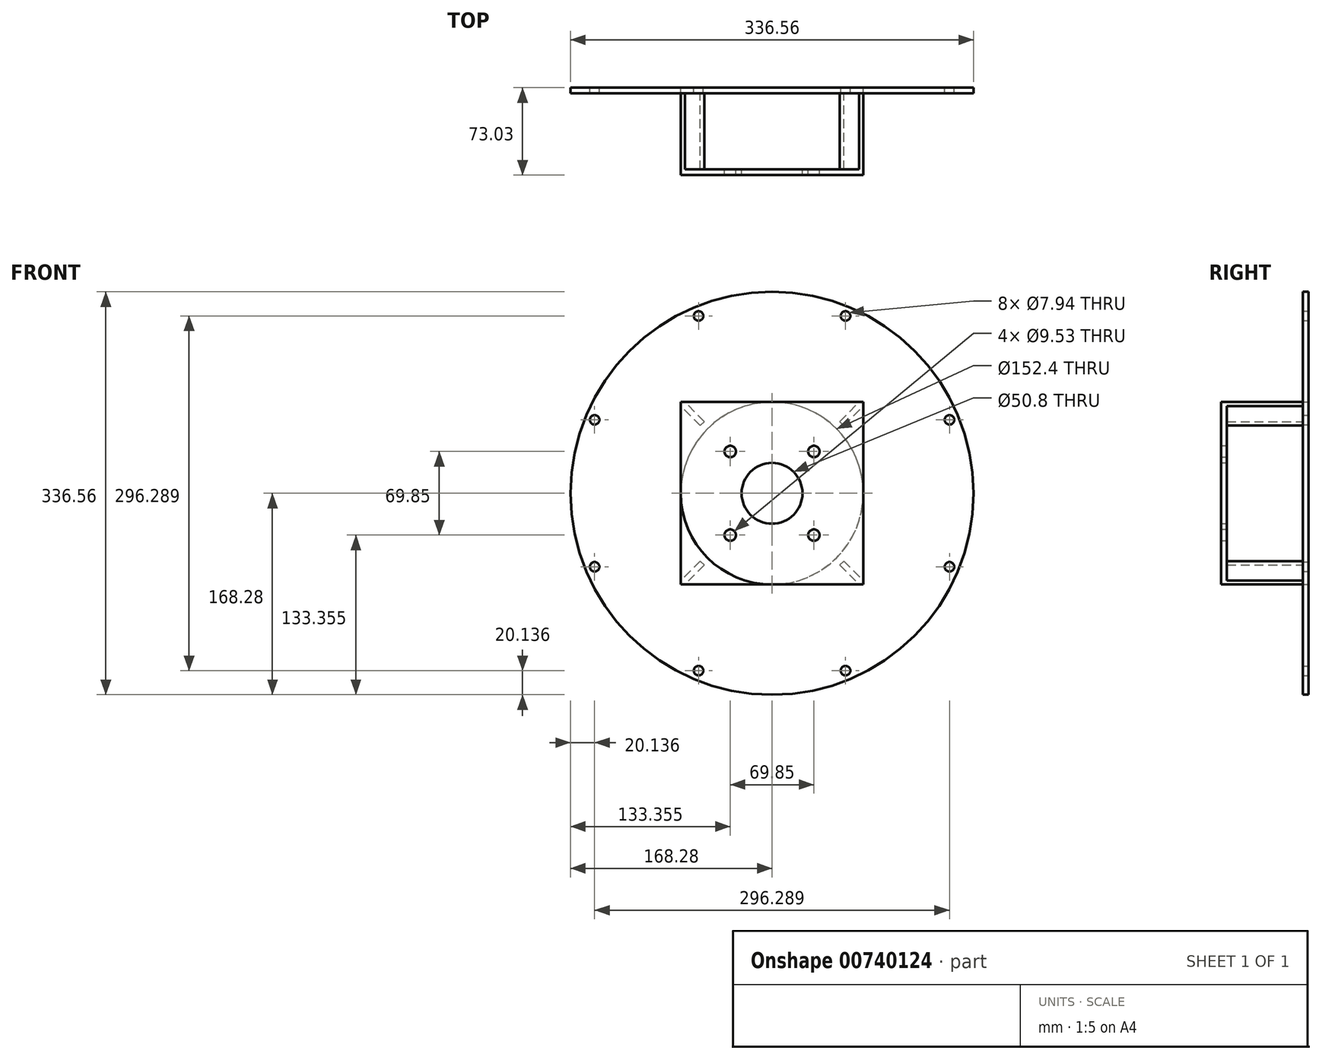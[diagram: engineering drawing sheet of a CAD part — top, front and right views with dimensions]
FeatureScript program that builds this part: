
annotation { "Feature Type Name" : "Feature", "Feature Type Description" : "" }
export const myFeature = defineFeature(function(context is Context, id is Id, definition is map)
    precondition{}
    {
        {
            var Q0;
            Q0=qCreatedBy(makeId("Front.planeOp"),FACE);
            var sketch = newSketch(context, id + "F0", { "sketchPlane" : qUnion([Q0])});
            skCircle(sketch, "E0", {"center": v(0, 0) * mm, "radius": 76.2 * mm});
            skCircle(sketch, "E1", {"center": v(0, 0) * mm, "radius": 152.4 * mm});
            skCircle(sketch, "E2", {"center": v(0, 0) * mm, "radius": 168.28 * mm});
            skLineSegment(sketch, "E3", {"start": v(0, 0) * mm, "end": v(0, -168.28) * mm});
            skLineSegment(sketch, "E4", {"start": v(64.4, -155.47) * mm, "end": v(61.36, -148.14) * mm});
            skCircle(sketch, "E5", {"center": v(61.36, -148.14) * mm, "radius": 3.97 * mm});
            skCircle(sketch, "E6.1.0", {"center": v(148.14, -61.36) * mm, "radius": 3.97 * mm});
            skCircle(sketch, "E6.2.0", {"center": v(148.14, 61.36) * mm, "radius": 3.97 * mm});
            skCircle(sketch, "E6.3.0", {"center": v(61.36, 148.14) * mm, "radius": 3.97 * mm});
            skCircle(sketch, "E6.4.0", {"center": v(-61.36, 148.14) * mm, "radius": 3.97 * mm});
            skCircle(sketch, "E6.5.0", {"center": v(-148.14, 61.36) * mm, "radius": 3.97 * mm});
            skCircle(sketch, "E6.6.0", {"center": v(-148.14, -61.36) * mm, "radius": 3.97 * mm});
            skCircle(sketch, "E6.7.0", {"center": v(-61.36, -148.14) * mm, "radius": 3.97 * mm});
            skSolve(sketch);
        }
        {
            var Q0;
            Q0=makeQuery(id+"F0.imprint","IMPRINT",FACE,{"disambiguationData":[TD([[makeQuery(id+"F0.imprint","IMPRINT",EDGE,{"derivedFrom":sQuery(id+"F0.wireOp",EDGE,"E1")}),-1.0]])]});
            var Q1;
            Q1=makeQuery(id+"F0.imprint","IMPRINT",FACE,{"disambiguationData":[TD([[makeQuery(id+"F0.imprint","IMPRINT",EDGE,{"derivedFrom":sQuery(id+"F0.wireOp",EDGE,"E0")}),-1.0]])]});
            extrude(context, id + "F1", {"entities" : qUnion([Q0, Q1]), "depth" : 4.76 * mm, "offsetDistance" : 25.4 * mm});
        }
        {
            var Q0;
            Q0=makeQuery(id+"F1.opExtrude","CAP_FACE",FACE,{"disambiguationData":[OSD([sQuery(id+"F0.wireOp",EDGE,"E0"),sQuery(id+"F0.wireOp",EDGE,"E2"),sQuery(id+"F0.wireOp",EDGE,"E5"),sQuery(id+"F0.wireOp",EDGE,"E6.1.0"),sQuery(id+"F0.wireOp",EDGE,"E6.2.0"),sQuery(id+"F0.wireOp",EDGE,"E6.3.0"),sQuery(id+"F0.wireOp",EDGE,"E6.4.0"),sQuery(id+"F0.wireOp",EDGE,"E6.5.0"),sQuery(id+"F0.wireOp",EDGE,"E6.6.0"),sQuery(id+"F0.wireOp",EDGE,"E6.7.0")])],"isStart":false});
            var sketch = newSketch(context, id + "F2", { "sketchPlane" : qUnion([Q0])});
            skLineSegment(sketch, "E7", {"start": v(0, 0) * mm, "end": v(76.2, 0) * mm});
            skLineSegment(sketch, "E8", {"start": v(76.2, 0) * mm, "end": v(76.2, 76.2) * mm});
            skLineSegment(sketch, "E9", {"start": v(76.2, 76.2) * mm, "end": v(-76.2, 76.2) * mm});
            skLineSegment(sketch, "E10", {"start": v(-76.2, 76.2) * mm, "end": v(-76.2, -76.2) * mm});
            skLineSegment(sketch, "E11", {"start": v(-76.2, -76.2) * mm, "end": v(76.2, -76.2) * mm});
            skLineSegment(sketch, "E12", {"start": v(76.2, -76.2) * mm, "end": v(76.2, 0) * mm});
            skLineSegment(sketch, "E13", {"start": v(-58.24, 58.24) * mm, "end": v(-56.56, 59.92) * mm});
            skLineSegment(sketch, "E14", {"start": v(-56.56, 59.92) * mm, "end": v(-72.83, 76.2) * mm});
            skLineSegment(sketch, "E15", {"start": v(-58.24, 58.24) * mm, "end": v(-59.92, 56.56) * mm});
            skLineSegment(sketch, "E16", {"start": v(-59.92, 56.56) * mm, "end": v(-76.2, 72.83) * mm});
            skLineSegment(sketch, "E17.1.0", {"start": v(-59.92, -56.56) * mm, "end": v(-76.2, -72.83) * mm});
            skLineSegment(sketch, "E17.1.1", {"start": v(-56.56, -59.92) * mm, "end": v(-72.83, -76.2) * mm});
            skLineSegment(sketch, "E17.1.2", {"start": v(-58.24, -58.24) * mm, "end": v(-56.56, -59.92) * mm});
            skLineSegment(sketch, "E17.1.3", {"start": v(-58.24, -58.24) * mm, "end": v(-59.92, -56.56) * mm});
            skLineSegment(sketch, "E17.2.0", {"start": v(56.56, -59.92) * mm, "end": v(72.83, -76.2) * mm});
            skLineSegment(sketch, "E17.2.1", {"start": v(59.92, -56.56) * mm, "end": v(76.2, -72.83) * mm});
            skLineSegment(sketch, "E17.2.2", {"start": v(58.24, -58.24) * mm, "end": v(59.92, -56.56) * mm});
            skLineSegment(sketch, "E17.2.3", {"start": v(58.24, -58.24) * mm, "end": v(56.56, -59.92) * mm});
            skLineSegment(sketch, "E17.3.0", {"start": v(59.92, 56.56) * mm, "end": v(76.2, 72.83) * mm});
            skLineSegment(sketch, "E17.3.1", {"start": v(56.56, 59.92) * mm, "end": v(72.83, 76.2) * mm});
            skLineSegment(sketch, "E17.3.2", {"start": v(58.24, 58.24) * mm, "end": v(56.56, 59.92) * mm});
            skLineSegment(sketch, "E17.3.3", {"start": v(58.24, 58.24) * mm, "end": v(59.92, 56.56) * mm});
            skPoint(sketch, "E17.center", {"position": v(0, 0) * mm});
            skSolve(sketch);
        }
        {
            var Q0;
            Q0=makeQuery(id+"F2.imprint","IMPRINT",FACE,{"disambiguationData":[TD([[makeQuery(id+"F2.imprint","IMPRINT",EDGE,{"derivedFrom":sQuery(id+"F2.wireOp",EDGE,"E13")}),1.0]])]});
            var Q1;
            {var subQ1=sQuery(id+"F2.wireOp",EDGE,"E17.3.0");Q1=makeQuery(id+"F2.imprint","IMPRINT",FACE,{"disambiguationData":[TD([[makeQuery(id+"F2.imprint","IMPRINT",EDGE,{"derivedFrom":subQ1}),1.0]])]});}
            var Q2;
            {var subQ4=sQuery(id+"F2.wireOp",EDGE,"E17.2.0");Q2=makeQuery(id+"F2.imprint","IMPRINT",FACE,{"disambiguationData":[TD([[makeQuery(id+"F2.imprint","IMPRINT",EDGE,{"derivedFrom":subQ4}),1.0]])]});}
            var Q3;
            {var subQ4=sQuery(id+"F2.wireOp",EDGE,"E17.1.0");Q3=makeQuery(id+"F2.imprint","IMPRINT",FACE,{"disambiguationData":[TD([[makeQuery(id+"F2.imprint","IMPRINT",EDGE,{"derivedFrom":subQ4}),1.0]])]});}
            extrude(context, id + "F3", {"entities" : qUnion([Q0, Q1, Q2, Q3]), "operationType" : NewBodyOperationType.ADD, "depth" : 63.5 * mm, "offsetDistance" : 25.4 * mm});
        }
        {
            var Q0;
            Q0=makeQuery(id+"F3.opExtrude","CAP_FACE",FACE,{"disambiguationData":[OSD([sQuery(id+"F2.wireOp",EDGE,"E9"),sQuery(id+"F2.wireOp",EDGE,"E10"),sQuery(id+"F2.wireOp",EDGE,"E13"),sQuery(id+"F2.wireOp",EDGE,"E14"),sQuery(id+"F2.wireOp",EDGE,"E15"),sQuery(id+"F2.wireOp",EDGE,"E16")])],"isStart":false});
            var sketch = newSketch(context, id + "F4", { "sketchPlane" : qUnion([Q0])});
            skLineSegment(sketch, "E18", {"start": v(-76.2, 76.2) * mm, "end": v(-76.2, -76.2) * mm});
            skLineSegment(sketch, "E19", {"start": v(-76.2, -76.2) * mm, "end": v(76.2, -76.2) * mm});
            skLineSegment(sketch, "E20", {"start": v(76.2, -76.2) * mm, "end": v(76.2, 76.2) * mm});
            skLineSegment(sketch, "E21", {"start": v(76.2, 76.2) * mm, "end": v(-76.2, 76.2) * mm});
            skCircle(sketch, "E22", {"center": v(0, 0) * mm, "radius": 25.4 * mm});
            skLineSegment(sketch, "E23", {"start": v(0, 0) * mm, "end": v(34.93, 0) * mm});
            skLineSegment(sketch, "E24", {"start": v(34.93, 0) * mm, "end": v(34.93, 34.93) * mm});
            skCircle(sketch, "E25", {"center": v(34.93, 34.93) * mm, "radius": 4.76 * mm});
            skCircle(sketch, "E26.1.0", {"center": v(-34.93, 34.93) * mm, "radius": 4.76 * mm});
            skCircle(sketch, "E26.2.0", {"center": v(-34.93, -34.92) * mm, "radius": 4.76 * mm});
            skCircle(sketch, "E26.3.0", {"center": v(34.92, -34.93) * mm, "radius": 4.76 * mm});
            skSolve(sketch);
        }
        {
            var Q0;
            {var subQ0=makeQuery(id+"F3.opExtrude","CAP_EDGE",EDGE,{"disambiguationData":[OSD([sQuery(id+"F2.wireOp",EDGE,"E14")])],"isStart":false});Q0=makeQuery(id+"F4.imprint","IMPRINT",FACE,{"disambiguationData":[TD([[makeQuery(id+"F4.imprint","IMPRINT",EDGE,{"derivedFrom":subQ0}),1.0]])]});}
            var Q1;
            {var subQ3=sQuery(id+"F4.wireOp",EDGE,"E19");Q1=makeQuery(id+"F4.imprint","IMPRINT",FACE,{"disambiguationData":[TD([[makeQuery(id+"F4.imprint","IMPRINT",EDGE,{"derivedFrom":subQ3}),1.0]])]});}
            extrude(context, id + "F5", {"entities" : qUnion([Q0, Q1]), "operationType" : NewBodyOperationType.ADD, "depth" : 4.76 * mm, "offsetDistance" : 25.4 * mm});
        }
    });
